# Revit family: QUADRATE NEON FLEX RGBX 1312_NDFXRGBX
name_source: partatom
category: Luminarias
units: mm (PartAtom-declared; Revit-internal decimal feet)

## family parameters
Compartido = No
Corte con vacíos al cargar = No
Cota de conector redondo = Diámetro de uso
Origen de luz = Sí
Punto de cálculo de habitación = No
Se basa en plano de trabajo = Sí
Siempre vertical = No
Tipo de pieza = Normal

## types (1)
- QUADRATE NEON FLEX RGBX 1312_NDFXRGBX
    Altura = 12 mm  [stored 0.0393701 ft]
    Ancho = 13 mm
    Cambio de temperatura de color de luz atenuada = <Ninguno>
    Comentarios de vataje = 24V
    Descripción = TIRA QUADRATE NEON FLEX RGBX 1312 DE PLASTICO FLEXIBLE CON UNA POTENCIA DE 20.2W/M DE UN TIPO DE LED 2835 SMD, USO PARA EXTERIORES IP67, IK08, TECNOLOGIA EN RGBX R 620-630nm G 525-530nm B 465-470nm, PRESENTACION DE 5M, CORTE 7.14CM, AMPERAJE 0.75A, ALIMENTADO A 24V, REQUIERE ACCESORIOS.
    Elevación por defecto = 0 mm  [stored 0 ft]
    Fabricante = BRILLANT
    Filtro de color = 16777215
    Longitud de línea de emisión = 600 mm
    Longitud de símbolo de origen de luz = 1500 mm  [stored 4.92126 ft]
    Marca = BRILLANT
    Modelo = NDFXRGBX
    Modelo Lampara = 2835 SMD
    Ángulo de campo de foco = 90.00°
    Ángulo de enfoque = 30.00°
    Ángulo de inclinación = 60.00°

note: [stored X ft] marks values corroborated as IEEE doubles in the binary element streams (Revit-internal decimal feet)

## geometry (parser evidence)
native form markers: Blend x2
no freeform markers — native parametric forms only
